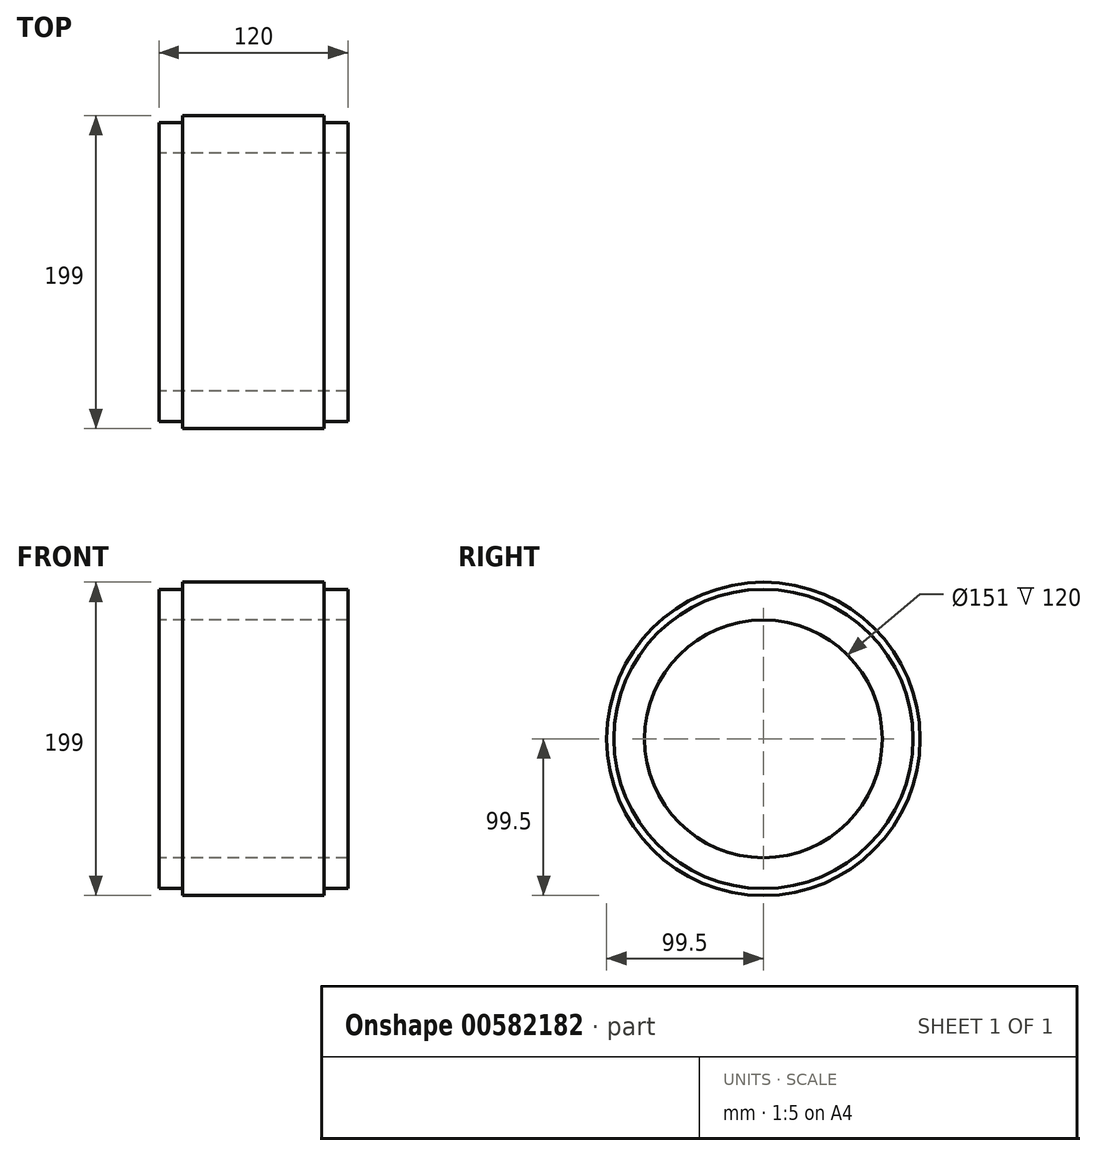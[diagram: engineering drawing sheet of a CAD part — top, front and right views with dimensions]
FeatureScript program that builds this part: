
annotation { "Feature Type Name" : "Feature", "Feature Type Description" : "" }
export const myFeature = defineFeature(function(context is Context, id is Id, definition is map)
    precondition{}
    {
        {
            var Q0;
            Q0=qCreatedBy(makeId("Front.planeOp"),FACE);
            var sketch = newSketch(context, id + "F0", { "sketchPlane" : qUnion([Q0])});
            skLineSegment(sketch, "E0", {"start": v(0, 75.5) * mm, "end": v(0, 95) * mm});
            skLineSegment(sketch, "E1", {"start": v(0, 95) * mm, "end": v(15, 95) * mm});
            skLineSegment(sketch, "E2", {"start": v(15, 95) * mm, "end": v(15, 99.5) * mm});
            skLineSegment(sketch, "E3", {"start": v(15, 99.5) * mm, "end": v(105, 99.5) * mm});
            skLineSegment(sketch, "E4", {"start": v(105, 99.5) * mm, "end": v(105, 95) * mm});
            skLineSegment(sketch, "E5", {"start": v(105, 95) * mm, "end": v(120, 95) * mm});
            skLineSegment(sketch, "E6", {"start": v(120, 95) * mm, "end": v(120, 75.5) * mm});
            skLineSegment(sketch, "E7", {"start": v(120, 75.5) * mm, "end": v(0, 75.5) * mm});
            skLineSegment(sketch, "E8", {"start": v(0, 0) * mm, "end": v(120, 0) * mm, "construction": true});
            skSolve(sketch);
        }
        {
            var Q0;
            Q0=qSketchRegion(id+"F0",true);
            var Q1;
            Q1=sQuery(id+"F0.wireOp",EDGE,"E8");
            revolve(context, id + "F1", {"entities" : qUnion([Q0]), "axis" : qUnion([Q1]), "revolveType" : RevolveType.FULL});
        }
    });
